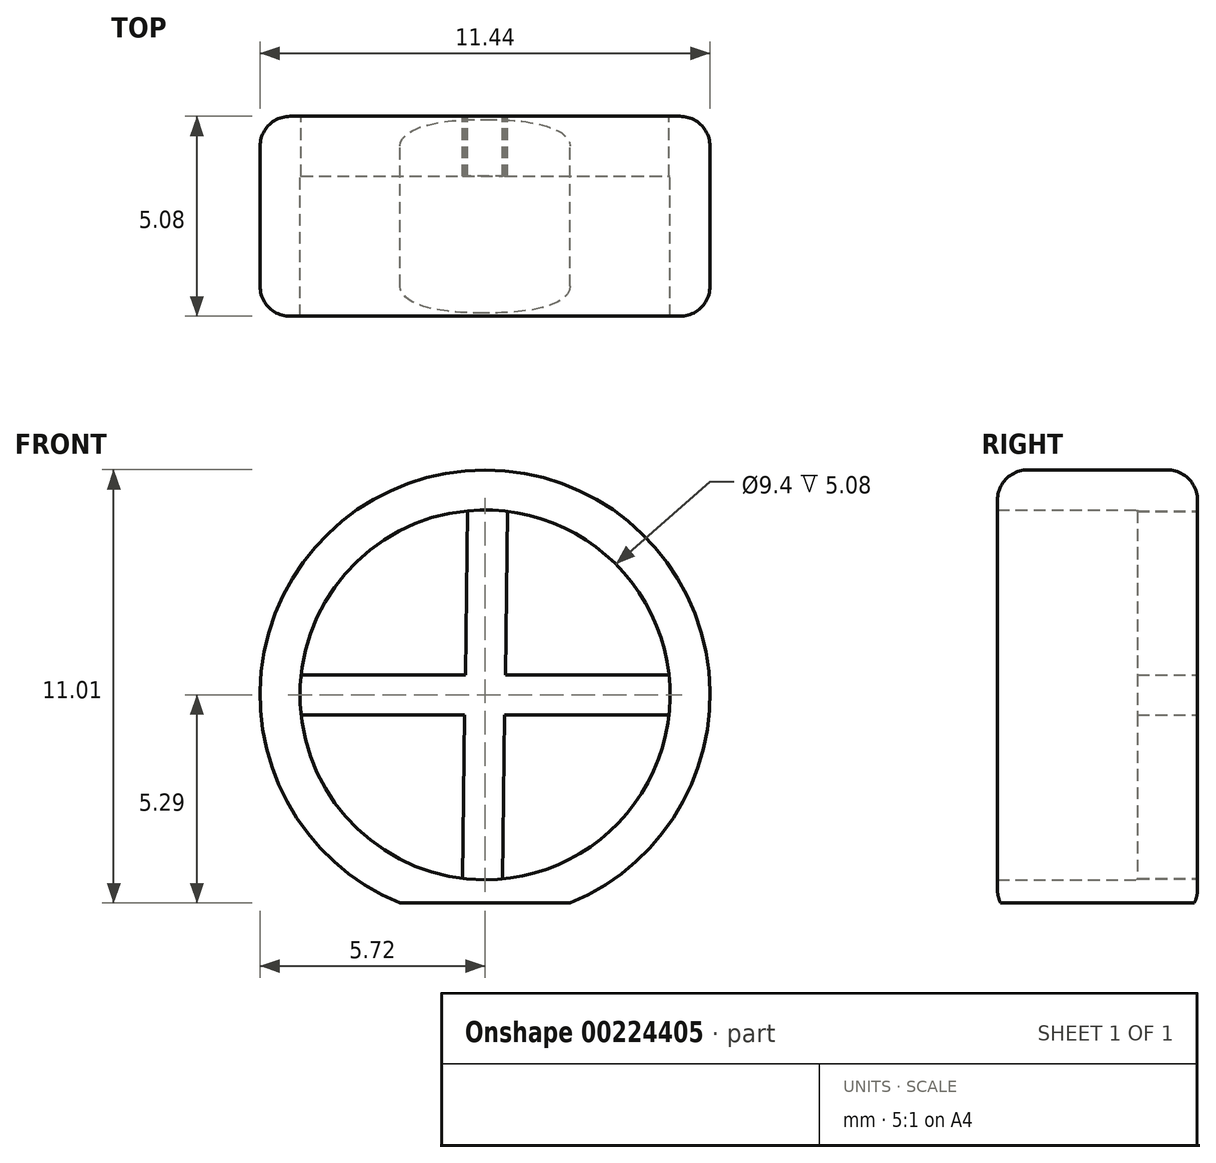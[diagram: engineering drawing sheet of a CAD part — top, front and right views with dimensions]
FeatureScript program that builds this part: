
annotation { "Feature Type Name" : "Feature", "Feature Type Description" : "" }
export const myFeature = defineFeature(function(context is Context, id is Id, definition is map)
    precondition{}
    {
        {
            var Q0;
            Q0=qCreatedBy(makeId("Front.planeOp"),FACE);
            var sketch = newSketch(context, id + "F0", { "sketchPlane" : qUnion([Q0])});
            skArc(sketch, "E0", {"start": v(2.16, -5.3) * mm, "mid": v(0, 5.71) * mm, "end": v(-2.16, -5.3) * mm});
            skCircle(sketch, "E1", {"center": v(0, 0) * mm, "radius": 4.7 * mm});
            skLineSegment(sketch, "E2.left", {"start": v(-0.45, 4.68) * mm, "end": v(-0.5, 0.5) * mm});
            skLineSegment(sketch, "E2.right", {"start": v(0.57, 4.66) * mm, "end": v(0.51, 0.5) * mm});
            skLineSegment(sketch, "E3.bottom", {"start": v(-4.67, 0.5) * mm, "end": v(-0.5, 0.5) * mm});
            skLineSegment(sketch, "E3.top", {"start": v(-4.67, -0.5) * mm, "end": v(-0.51, -0.5) * mm});
            skLineSegment(sketch, "E4.trimOffspring", {"start": v(0.51, 0.5) * mm, "end": v(4.67, 0.5) * mm});
            skLineSegment(sketch, "E5.trimOffspring", {"start": v(0.5, -0.5) * mm, "end": v(0.45, -4.68) * mm});
            skLineSegment(sketch, "E6.trimOffspring", {"start": v(0.5, -0.5) * mm, "end": v(4.67, -0.5) * mm});
            skLineSegment(sketch, "E7.trimOffspring", {"start": v(-0.51, -0.5) * mm, "end": v(-0.57, -4.66) * mm});
            skLineSegment(sketch, "E8", {"start": v(-2.16, -5.3) * mm, "end": v(2.16, -5.3) * mm});
            skSolve(sketch);
        }
        {
            var Q0;
            Q0=makeQuery(id+"F0.imprint","IMPRINT",FACE,{"disambiguationData":[TD([[makeQuery(id+"F0.imprint","IMPRINT",EDGE,{"derivedFrom":sQuery(id+"F0.wireOp",EDGE,"E0")}),1.0]])]});
            extrude(context, id + "F1", {"entities" : qUnion([Q0]), "depth" : 5.08 * mm});
        }
        {
            var Q0;
            {var subQ4=sQuery(id+"F0.wireOp",EDGE,"E2.left");Q0=makeQuery(id+"F0.imprint","IMPRINT",FACE,{"disambiguationData":[TD([[makeQuery(id+"F0.imprint","IMPRINT",EDGE,{"derivedFrom":subQ4}),1.0]])]});}
            extrude(context, id + "F2", {"entities" : qUnion([Q0]), "operationType" : NewBodyOperationType.ADD, "depth" : 1.52 * mm});
        }
        {
            var Q0;
            Q0=makeQuery(id+"F1.opExtrude","CAP_EDGE",EDGE,{"disambiguationData":[OSD([sQuery(id+"F0.wireOp",EDGE,"E0")])],"isStart":false});
            var Q1;
            Q1=makeQuery(id+"F1.opExtrude","CAP_EDGE",EDGE,{"disambiguationData":[OSD([sQuery(id+"F0.wireOp",EDGE,"E0")])],"isStart":true});
            fillet(context, id + "F3", {"entities" : qUnion([Q0, Q1]), "radius" : 0.76 * mm, "tangentPropagation" : true, "allowEdgeOverflow" : false});
        }
    });
